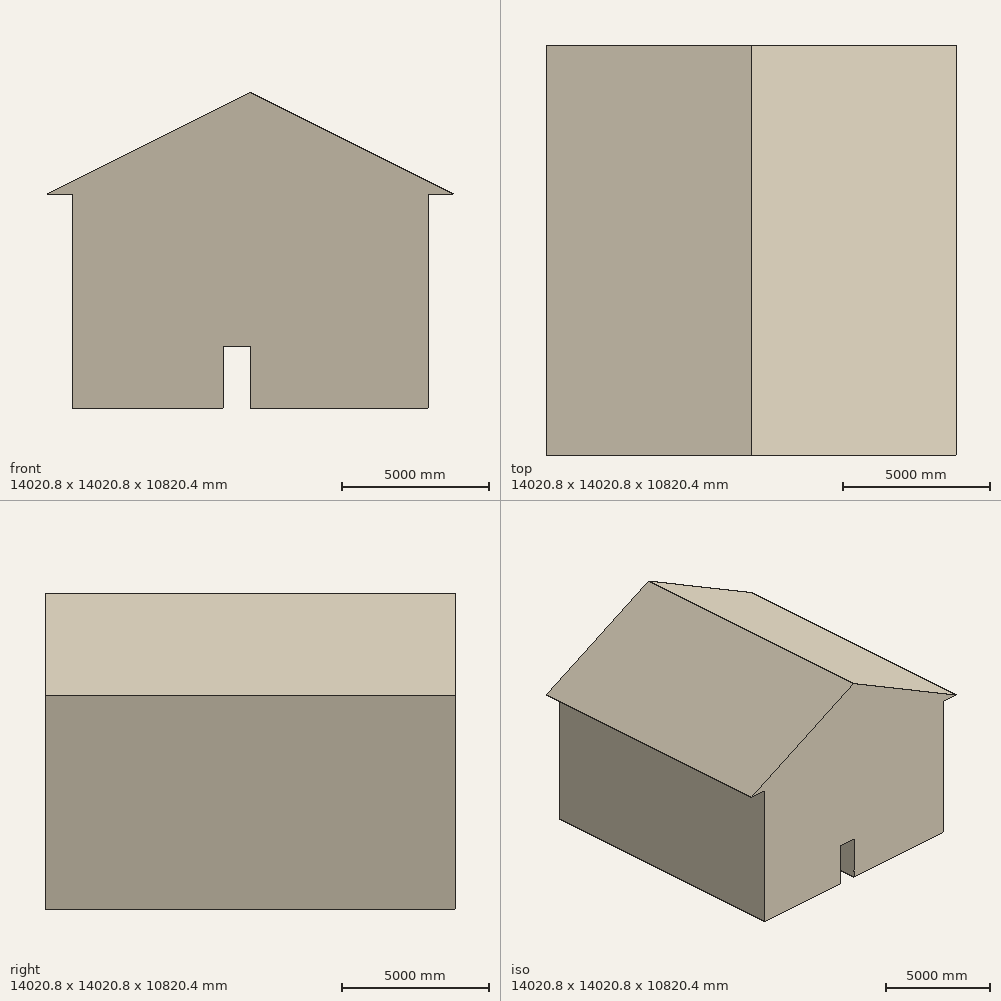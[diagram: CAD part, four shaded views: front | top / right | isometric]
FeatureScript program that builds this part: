
annotation { "Feature Type Name" : "Feature", "Feature Type Description" : "" }
export const myFeature = defineFeature(function(context is Context, id is Id, definition is map)
    precondition{}
    {
        {
            var Q0;
            Q0=qCreatedBy(makeId("Front.planeOp"),FACE);
            var sketch = newSketch(context, id + "F0", { "sketchPlane" : qUnion([Q0])});
            skLineSegment(sketch, "E0", {"start": v(0, 0) * mm, "end": v(-6096, 0) * mm});
            skLineSegment(sketch, "E1", {"start": v(0, 0) * mm, "end": v(6096, 0) * mm});
            skLineSegment(sketch, "E2", {"start": v(0, 0) * mm, "end": v(0, 3048) * mm});
            skLineSegment(sketch, "E3", {"start": v(0, 3048) * mm, "end": v(6096, 0) * mm});
            skLineSegment(sketch, "E4", {"start": v(0, 3048) * mm, "end": v(-6096, 0) * mm});
            skLineSegment(sketch, "E5", {"start": v(0, 3048) * mm, "end": v(0, 3505.2) * mm});
            skLineSegment(sketch, "E6", {"start": v(-6096, 0) * mm, "end": v(-7010.4, 0) * mm});
            skLineSegment(sketch, "E7", {"start": v(6096, 0) * mm, "end": v(7010.4, 0) * mm});
            skLineSegment(sketch, "E8", {"start": v(0, 3505.2) * mm, "end": v(-7010.4, 0) * mm});
            skLineSegment(sketch, "E9", {"start": v(0, 3505.2) * mm, "end": v(7010.4, 0) * mm});
            skLineSegment(sketch, "E10", {"start": v(-6096, 0) * mm, "end": v(-6096, -7315.2) * mm});
            skLineSegment(sketch, "E11", {"start": v(-6096, -7315.2) * mm, "end": v(6096, -7315.2) * mm});
            skLineSegment(sketch, "E12", {"start": v(6096, -7315.2) * mm, "end": v(6096, 0) * mm});
            skLineSegment(sketch, "E13", {"start": v(-914.4, -7315.2) * mm, "end": v(-914.4, -5181.6) * mm});
            skLineSegment(sketch, "E14", {"start": v(-914.4, -5181.6) * mm, "end": v(0, -5181.6) * mm});
            skLineSegment(sketch, "E15", {"start": v(0, -5181.6) * mm, "end": v(0, -7315.2) * mm});
            skLineSegment(sketch, "E16", {"start": v(6096, -7315.2) * mm, "end": v(6096, -7924.8) * mm});
            skLineSegment(sketch, "E17", {"start": v(-6096, -7315.2) * mm, "end": v(-6096, -7924.8) * mm});
            skLineSegment(sketch, "E18", {"start": v(-6096, -7924.8) * mm, "end": v(6096, -7924.8) * mm});
            skSolve(sketch);
        }
        {
            var Q0;
            Q0=makeQuery(id+"F0.imprint","IMPRINT",FACE,{"disambiguationData":[TD([[makeQuery(id+"F0.imprint","IMPRINT",EDGE,{"derivedFrom":sQuery(id+"F0.wireOp",EDGE,"E4")}),-1.0]])]});
            var Q1;
            Q1=makeQuery(id+"F0.imprint","IMPRINT",FACE,{"disambiguationData":[TD([[makeQuery(id+"F0.imprint","IMPRINT",EDGE,{"derivedFrom":sQuery(id+"F0.wireOp",EDGE,"E3")}),1.0]])]});
            var Q2;
            Q2=makeQuery(id+"F0.imprint","IMPRINT",FACE,{"disambiguationData":[TD([[makeQuery(id+"F0.imprint","IMPRINT",EDGE,{"derivedFrom":sQuery(id+"F0.wireOp",EDGE,"E0")}),1.0]])]});
            var Q3;
            Q3=makeQuery(id+"F0.imprint","IMPRINT",FACE,{"disambiguationData":[TD([[makeQuery(id+"F0.imprint","IMPRINT",EDGE,{"derivedFrom":sQuery(id+"F0.wireOp",EDGE,"E1")}),1.0]])]});
            var Q4;
            Q4=makeQuery(id+"F0.imprint","IMPRINT",FACE,{"disambiguationData":[TD([[makeQuery(id+"F0.imprint","IMPRINT",EDGE,{"derivedFrom":sQuery(id+"F0.wireOp",EDGE,"E0")}),-1.0]])]});
            extrude(context, id + "F1", {"entities" : qUnion([Q0, Q1, Q2, Q3, Q4]), "depth" : 14020.8 * mm, "offsetDistance" : 30.48 * mm});
        }
    });
